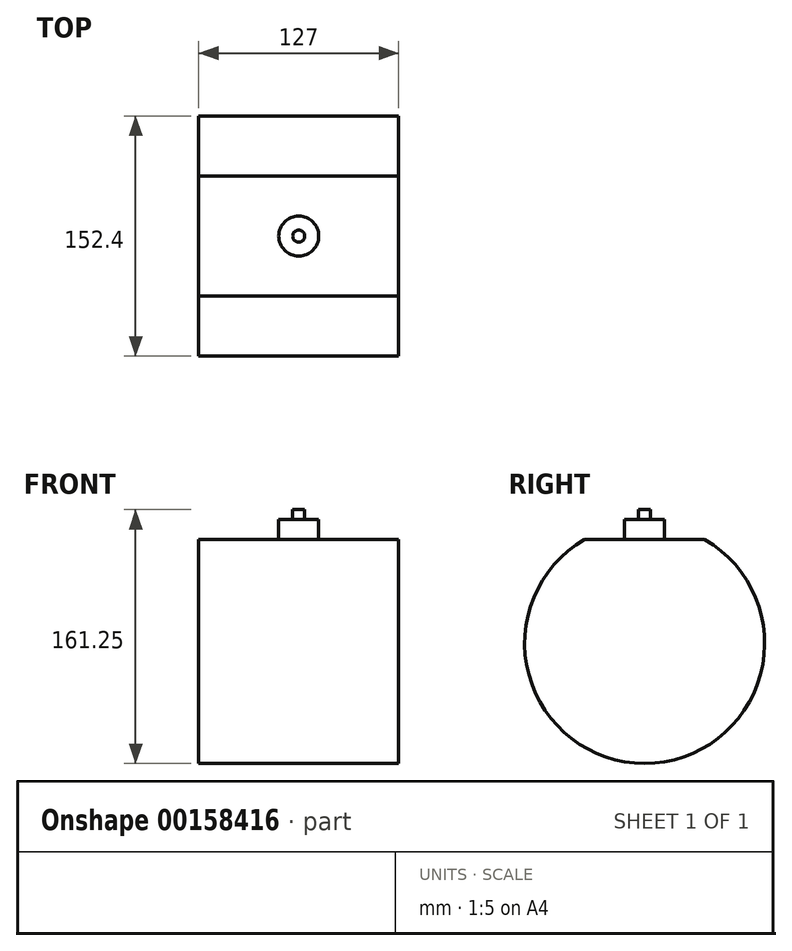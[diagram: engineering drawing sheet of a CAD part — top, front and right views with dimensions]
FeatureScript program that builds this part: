
annotation { "Feature Type Name" : "Feature", "Feature Type Description" : "" }
export const myFeature = defineFeature(function(context is Context, id is Id, definition is map)
    precondition{}
    {
        {
            var Q0;
            Q0=qCreatedBy(makeId("Right.planeOp"),FACE);
            var sketch = newSketch(context, id + "F0", { "sketchPlane" : qUnion([Q0])});
            skLineSegment(sketch, "E0", {"start": v(-59.54, 68.6) * mm, "end": v(16.66, 68.6) * mm});
            skArc(sketch, "E1", {"start": v(-59.54, 68.6) * mm, "mid": v(-21.44, -73.6) * mm, "end": v(16.66, 68.6) * mm});
            skSolve(sketch);
        }
        {
            var Q0;
            Q0=makeQuery(id+"F0.imprint","IMPRINT",FACE,{"disambiguationData":[TD([[makeQuery(id+"F0.imprint","IMPRINT",EDGE,{"derivedFrom":sQuery(id+"F0.wireOp",EDGE,"E0")}),-1.0]])]});
            extrude(context, id + "F1", {"entities" : qUnion([Q0]), "depth" : 127 * mm});
        }
        {
            var Q0;
            Q0=makeQuery(id+"F1.opExtrude","SWEPT_FACE",FACE,{"disambiguationData":[OSD([sQuery(id+"F0.wireOp",EDGE,"E0")])]});
            var sketch = newSketch(context, id + "F2", { "sketchPlane" : qUnion([Q0])});
            skCircle(sketch, "E2", {"center": v(63.5, -21.44) * mm, "radius": 12.7 * mm});
            skPoint(sketch, "E2.centerSnap0", {"position": v(63.5, -59.54) * mm});
            skPoint(sketch, "E2.centerSnap1", {"position": v(127, -21.44) * mm});
            skSolve(sketch);
        }
        {
            var Q0;
            Q0=makeQuery(id+"F2.imprint","IMPRINT",FACE,{"disambiguationData":[TD([[makeQuery(id+"F2.imprint","IMPRINT",EDGE,{"derivedFrom":sQuery(id+"F2.wireOp",EDGE,"E2")}),1.0]])]});
            extrude(context, id + "F3", {"entities" : qUnion([Q0]), "operationType" : NewBodyOperationType.ADD, "depth" : 12.7 * mm});
        }
        {
            var Q0;
            Q0=makeQuery(id+"F3.opExtrude","CAP_FACE",FACE,{"disambiguationData":[OSD([sQuery(id+"F2.wireOp",EDGE,"E2")])],"isStart":false});
            var sketch = newSketch(context, id + "F4", { "sketchPlane" : qUnion([Q0])});
            skCircle(sketch, "E3", {"center": v(63.5, -21.44) * mm, "radius": 3.81 * mm});
            skSolve(sketch);
        }
        {
            var Q0;
            Q0=makeQuery(id+"F4.imprint","IMPRINT",FACE,{"disambiguationData":[TD([[makeQuery(id+"F4.imprint","IMPRINT",EDGE,{"derivedFrom":sQuery(id+"F4.wireOp",EDGE,"E3")}),1.0]])]});
            extrude(context, id + "F5", {"entities" : qUnion([Q0]), "operationType" : NewBodyOperationType.ADD, "depth" : 6.35 * mm});
        }
    });
